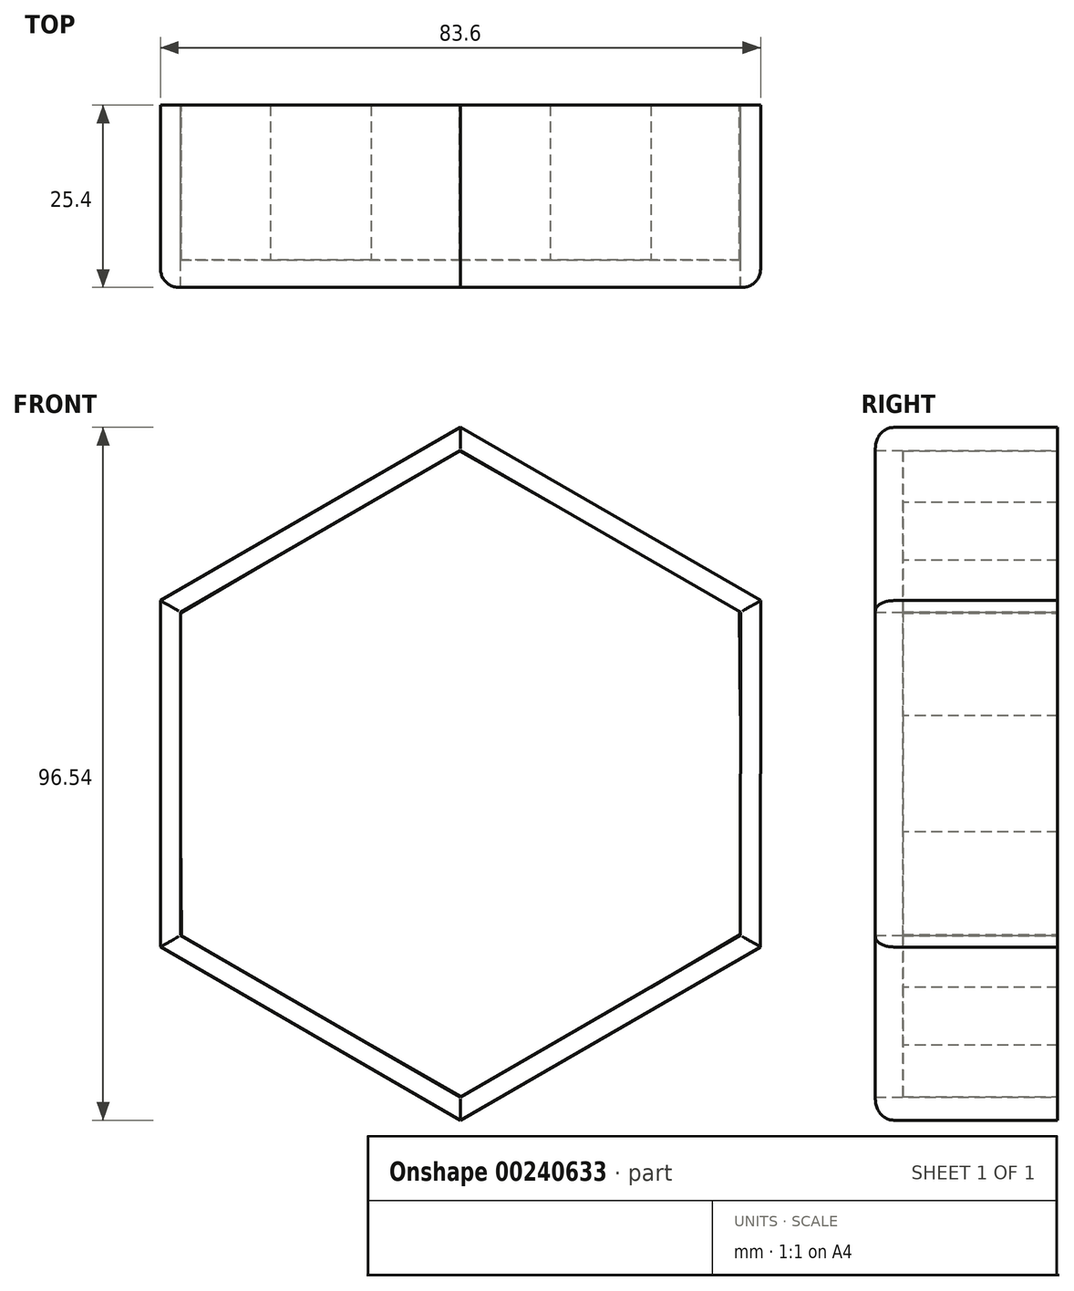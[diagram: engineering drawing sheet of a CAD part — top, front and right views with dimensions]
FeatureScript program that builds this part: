
annotation { "Feature Type Name" : "Feature", "Feature Type Description" : "" }
export const myFeature = defineFeature(function(context is Context, id is Id, definition is map)
    precondition{}
    {
        {
            var Q0;
            Q0=qCreatedBy(makeId("Front.planeOp"),FACE);
            var sketch = newSketch(context, id + "F0", { "sketchPlane" : qUnion([Q0])});
            skCircle(sketch, "E0.cCircle", {"center": v(0, 0) * mm, "radius": 41.8 * mm, "construction": true});
            skLineSegment(sketch, "E0.0", {"start": v(-41.8, 24.14) * mm, "end": v(0, 48.27) * mm});
            skLineSegment(sketch, "E0.1", {"start": v(0, 48.27) * mm, "end": v(41.8, 24.13) * mm});
            skLineSegment(sketch, "E0.2", {"start": v(41.8, 24.13) * mm, "end": v(41.8, -24.14) * mm});
            skLineSegment(sketch, "E0.3", {"start": v(41.8, -24.14) * mm, "end": v(0, -48.27) * mm});
            skLineSegment(sketch, "E0.4", {"start": v(0, -48.27) * mm, "end": v(-41.8, -24.13) * mm});
            skLineSegment(sketch, "E0.5", {"start": v(-41.8, -24.13) * mm, "end": v(-41.8, 24.14) * mm});
            skPoint(sketch, "E0.0.midPoint", {"position": v(-20.9, 36.2) * mm});
            skCircle(sketch, "E1.cCircle", {"center": v(0, 0) * mm, "radius": 39 * mm, "construction": true});
            skLineSegment(sketch, "E1.0", {"start": v(0, 45.04) * mm, "end": v(39, 22.51) * mm});
            skLineSegment(sketch, "E1.1", {"start": v(39, 22.51) * mm, "end": v(39, -22.52) * mm});
            skLineSegment(sketch, "E1.2", {"start": v(39, -22.52) * mm, "end": v(0, -45.04) * mm});
            skLineSegment(sketch, "E1.3", {"start": v(0, -45.04) * mm, "end": v(-39, -22.51) * mm});
            skLineSegment(sketch, "E1.4", {"start": v(-39, -22.51) * mm, "end": v(-39, 22.52) * mm});
            skLineSegment(sketch, "E1.5", {"start": v(-39, 22.52) * mm, "end": v(0, 45.04) * mm});
            skPoint(sketch, "E1.0.midPoint", {"position": v(19.5, 33.78) * mm});
            skSolve(sketch);
        }
        {
            var Q0;
            Q0=makeQuery(id+"F0.imprint","IMPRINT",FACE,{"disambiguationData":[TD([[makeQuery(id+"F0.imprint","IMPRINT",EDGE,{"derivedFrom":sQuery(id+"F0.wireOp",EDGE,"E0.0")}),-1.0]])]});
            extrude(context, id + "F1", {"entities" : qUnion([Q0]), "depth" : 25.4 * mm});
        }
        {
            var Q0;
            Q0=qCreatedBy(makeId("Front.planeOp"),FACE);
            var sketch = newSketch(context, id + "F2", { "sketchPlane" : qUnion([Q0])});
            skCircle(sketch, "E2.cCircle", {"center": v(0, 0) * mm, "radius": 39.07 * mm, "construction": true});
            skLineSegment(sketch, "E2.0", {"start": v(-0.38, 45.11) * mm, "end": v(38.88, 22.9) * mm});
            skLineSegment(sketch, "E2.1", {"start": v(38.88, 22.9) * mm, "end": v(39.26, -22.22) * mm});
            skLineSegment(sketch, "E2.2", {"start": v(39.26, -22.22) * mm, "end": v(0.38, -45.11) * mm});
            skLineSegment(sketch, "E2.3", {"start": v(0.38, -45.11) * mm, "end": v(-38.88, -22.9) * mm});
            skLineSegment(sketch, "E2.4", {"start": v(-38.88, -22.9) * mm, "end": v(-39.26, 22.22) * mm});
            skLineSegment(sketch, "E2.5", {"start": v(-39.26, 22.22) * mm, "end": v(-0.38, 45.11) * mm});
            skPoint(sketch, "E2.0.midPoint", {"position": v(19.25, 34) * mm});
            skSolve(sketch);
        }
        {
            var Q0;
            Q0=makeQuery(id+"F2.imprint","IMPRINT",FACE,{"disambiguationData":[TD([[makeQuery(id+"F2.imprint","IMPRINT",EDGE,{"derivedFrom":sQuery(id+"F2.wireOp",EDGE,"E2.0")}),-1.0]])]});
            extrude(context, id + "F3", {"entities" : qUnion([Q0]), "operationType" : NewBodyOperationType.ADD, "depth" : 21.59 * mm});
        }
        {
            var Q0;
            Q0=makeQuery(id+"F1.opExtrude","CAP_EDGE",EDGE,{"disambiguationData":[OSD([sQuery(id+"F0.wireOp",EDGE,"E0.4")])],"isStart":false});
            var Q1;
            Q1=makeQuery(id+"F1.opExtrude","CAP_EDGE",EDGE,{"disambiguationData":[OSD([sQuery(id+"F0.wireOp",EDGE,"E0.5")])],"isStart":false});
            var Q2;
            Q2=makeQuery(id+"F1.opExtrude","CAP_EDGE",EDGE,{"disambiguationData":[OSD([sQuery(id+"F0.wireOp",EDGE,"E0.0")])],"isStart":false});
            var Q3;
            Q3=makeQuery(id+"F1.opExtrude","CAP_EDGE",EDGE,{"disambiguationData":[OSD([sQuery(id+"F0.wireOp",EDGE,"E0.3")])],"isStart":false});
            var Q4;
            Q4=makeQuery(id+"F1.opExtrude","CAP_EDGE",EDGE,{"disambiguationData":[OSD([sQuery(id+"F0.wireOp",EDGE,"E0.2")])],"isStart":false});
            var Q5;
            Q5=makeQuery(id+"F1.opExtrude","CAP_EDGE",EDGE,{"disambiguationData":[OSD([sQuery(id+"F0.wireOp",EDGE,"E0.1")])],"isStart":false});
            fillet(context, id + "F4", {"entities" : qUnion([Q0, Q1, Q2, Q3, Q4, Q5]), "radius" : 2.54 * mm, "tangentPropagation" : true, "allowEdgeOverflow" : false});
        }
    });
